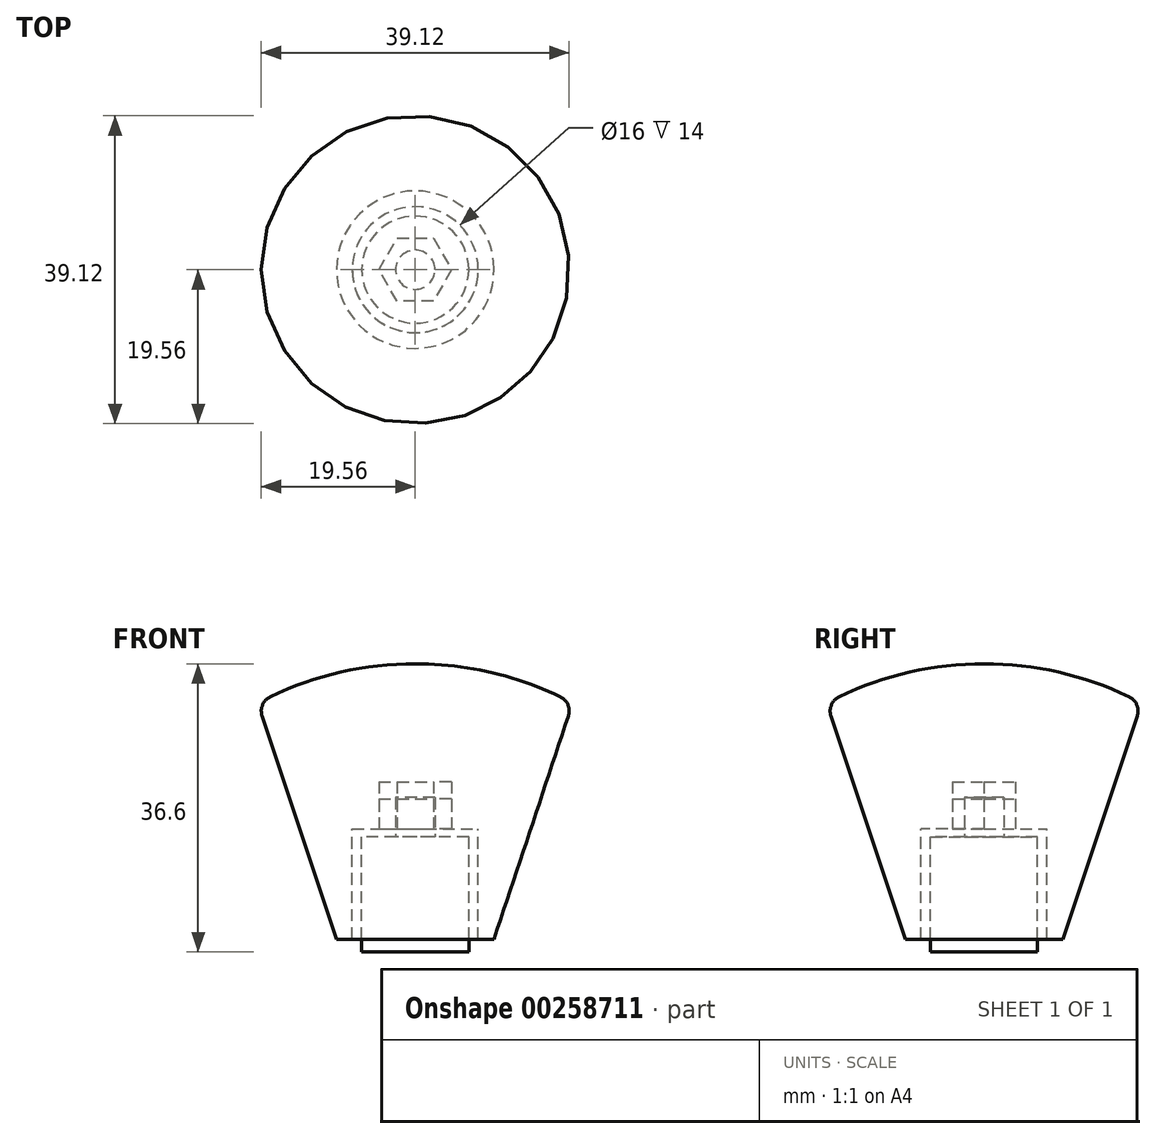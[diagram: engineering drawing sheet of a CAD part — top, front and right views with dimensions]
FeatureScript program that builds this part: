
annotation { "Feature Type Name" : "Feature", "Feature Type Description" : "" }
export const myFeature = defineFeature(function(context is Context, id is Id, definition is map)
    precondition{}
    {
        {
            var Q0;
            Q0=qCreatedBy(makeId("Top.planeOp"),FACE);
            var sketch = newSketch(context, id + "F0", { "sketchPlane" : qUnion([Q0])});
            skCircle(sketch, "E0", {"center": v(0, 0) * mm, "radius": 6.8 * mm});
            skCircle(sketch, "E1", {"center": v(0, 0) * mm, "radius": 2.5 * mm});
            skSolve(sketch);
        }
        {
            var Q0;
            Q0=makeQuery(id+"F0.imprint","IMPRINT",FACE,{"disambiguationData":[TD([[makeQuery(id+"F0.imprint","IMPRINT",EDGE,{"derivedFrom":sQuery(id+"F0.wireOp",EDGE,"E0")}),1.0]])]});
            var Q1;
            Q1=makeQuery(id+"F0.imprint","IMPRINT",FACE,{"disambiguationData":[TD([[makeQuery(id+"F0.imprint","IMPRINT",EDGE,{"derivedFrom":sQuery(id+"F0.wireOp",EDGE,"E1")}),1.0]])]});
            extrude(context, id + "F1", {"entities" : qUnion([Q0, Q1]), "oppositeDirection" : true, "depth" : 14.6 * mm});
        }
        {
            var Q0;
            Q0=makeQuery(id+"F0.imprint","IMPRINT",FACE,{"disambiguationData":[TD([[makeQuery(id+"F0.imprint","IMPRINT",EDGE,{"derivedFrom":sQuery(id+"F0.wireOp",EDGE,"E1")}),1.0]])]});
            extrude(context, id + "F2", {"entities" : qUnion([Q0]), "operationType" : NewBodyOperationType.ADD, "depth" : 5 * mm});
        }
        {
            var Q0;
            Q0=makeQuery(id+"F0.imprint","IMPRINT",FACE,{"disambiguationData":[TD([[makeQuery(id+"F0.imprint","IMPRINT",EDGE,{"derivedFrom":sQuery(id+"F0.wireOp",EDGE,"E0")}),1.0]])]});
            cPlane(context, id + "F3", {"entities" : qUnion([Q0]), "cplaneType" : CPlaneType.OFFSET, "offset" : 1 * mm, "width" : 150 * mm, "height" : 150 * mm});
        }
        {
            var Q0;
            Q0=qCreatedBy(id+"F3.planeOp",FACE);
            var sketch = newSketch(context, id + "F4", { "sketchPlane" : qUnion([Q0])});
            skCircle(sketch, "E2.cCircle", {"center": v(0, 0) * mm, "radius": 4 * mm, "construction": true});
            skLineSegment(sketch, "E2.0", {"start": v(-2.3, 4) * mm, "end": v(2.3, 4) * mm});
            skLineSegment(sketch, "E2.1", {"start": v(2.3, 4) * mm, "end": v(4.62, 0) * mm});
            skLineSegment(sketch, "E2.2", {"start": v(4.62, 0) * mm, "end": v(2.3, -4) * mm});
            skLineSegment(sketch, "E2.3", {"start": v(2.3, -4) * mm, "end": v(-2.3, -4) * mm});
            skLineSegment(sketch, "E2.4", {"start": v(-2.3, -4) * mm, "end": v(-4.62, 0) * mm});
            skLineSegment(sketch, "E2.5", {"start": v(-4.62, 0) * mm, "end": v(-2.3, 4) * mm});
            skPoint(sketch, "E2.0.midPoint", {"position": v(0, 4) * mm});
            skSolve(sketch);
        }
        {
            var Q0;
            Q0=makeQuery(id+"F4.imprint","IMPRINT",FACE,{"disambiguationData":[TD([[makeQuery(id+"F4.imprint","IMPRINT",EDGE,{"derivedFrom":sQuery(id+"F4.wireOp",EDGE,"E2.0")}),-1.0]])]});
            extrude(context, id + "F5", {"entities" : qUnion([Q0]), "depth" : 3.8 * mm});
        }
        {
            var Q0;
            Q0=makeQuery(id+"F5.opExtrude","CAP_FACE",FACE,{"disambiguationData":[OSD([sQuery(id+"F4.wireOp",EDGE,"E2.0"),sQuery(id+"F4.wireOp",EDGE,"E2.1"),sQuery(id+"F4.wireOp",EDGE,"E2.2"),sQuery(id+"F4.wireOp",EDGE,"E2.3"),sQuery(id+"F4.wireOp",EDGE,"E2.4"),sQuery(id+"F4.wireOp",EDGE,"E2.5")])],"isStart":true});
            var sketch = newSketch(context, id + "F6", { "sketchPlane" : qUnion([Q0])});
            skLineSegment(sketch, "E3.0.0", {"start": v(-2.3, -4) * mm, "end": v(-4.62, 0) * mm});
            skLineSegment(sketch, "E3.0.1", {"start": v(-4.62, 0) * mm, "end": v(-2.3, 4) * mm});
            skLineSegment(sketch, "E3.0.2", {"start": v(-2.3, 4) * mm, "end": v(2.3, 4) * mm});
            skLineSegment(sketch, "E3.0.3", {"start": v(2.3, 4) * mm, "end": v(4.62, 0) * mm});
            skLineSegment(sketch, "E3.0.4", {"start": v(4.62, 0) * mm, "end": v(2.3, -4) * mm});
            skLineSegment(sketch, "E3.0.5", {"start": v(2.3, -4) * mm, "end": v(-2.3, -4) * mm});
            skCircle(sketch, "E4", {"center": v(0, 0) * mm, "radius": 8 * mm});
            skSolve(sketch);
        }
        {
            var Q0;
            Q0=makeQuery(id+"F6.imprint","IMPRINT",FACE,{"disambiguationData":[TD([[makeQuery(id+"F6.imprint","IMPRINT",EDGE,{"derivedFrom":sQuery(id+"F6.wireOp",EDGE,"E3.0.0")}),-1.0]])]});
            extrude(context, id + "F7", {"entities" : qUnion([Q0]), "oppositeDirection" : true, "depth" : 6 * mm});
        }
        {
            var Q0;
            Q0=makeQuery(id+"F1.opExtrude","CAP_FACE",FACE,{"disambiguationData":[OSD([sQuery(id+"F0.wireOp",EDGE,"E0")])],"isStart":true});
            cPlane(context, id + "F8", {"entities" : qUnion([Q0]), "cplaneType" : CPlaneType.OFFSET, "offset" : 13 * mm, "oppositeDirection" : true, "width" : 150 * mm, "height" : 150 * mm});
        }
        {
            var Q0;
            Q0=qCreatedBy(id+"F8.planeOp",FACE);
            var sketch = newSketch(context, id + "F9", { "sketchPlane" : qUnion([Q0])});
            skCircle(sketch, "E5.0", {"center": v(0, 0) * mm, "radius": 8 * mm});
            skSolve(sketch);
        }
        {
            var Q0;
            Q0=qCreatedBy(makeId("Front.planeOp"),FACE);
            var sketch = newSketch(context, id + "F10", { "sketchPlane" : qUnion([Q0])});
            skLineSegment(sketch, "E6.0", {"start": v(8, 7) * mm, "end": v(-8, 7) * mm});
            skLineSegment(sketch, "E7.0", {"start": v(-8, -13) * mm, "end": v(8, -13) * mm});
            skArc(sketch, "E8", {"start": v(20, 17) * mm, "mid": v(10.3, 20.73) * mm, "end": v(0, 22) * mm});
            skLineSegment(sketch, "E9", {"start": v(0, 26.7) * mm, "end": v(0, -17.97) * mm, "construction": true});
            skLineSegment(sketch, "E10", {"start": v(8, -13) * mm, "end": v(8, 7) * mm});
            skLineSegment(sketch, "E11", {"start": v(-8, 7) * mm, "end": v(-8, -13) * mm});
            skLineSegment(sketch, "E12", {"start": v(8, -13) * mm, "end": v(10, -13) * mm});
            skLineSegment(sketch, "E13", {"start": v(10, -13) * mm, "end": v(20, 17) * mm});
            skPoint(sketch, "E14", {"position": v(0, 22) * mm});
            skLineSegment(sketch, "E15", {"start": v(20, 17) * mm, "end": v(0, 17) * mm, "construction": true});
            skLineSegment(sketch, "E16", {"start": v(0, 22) * mm, "end": v(0, 7) * mm});
            skSolve(sketch);
        }
        {
            var Q0;
            Q0=makeQuery(id+"F10.imprint","IMPRINT",FACE,{"disambiguationData":[TD([[makeQuery(id+"F10.imprint","IMPRINT",EDGE,{"derivedFrom":sQuery(id+"F10.wireOp",EDGE,"E8")}),1.0]])]});
            var Q1;
            Q1=sQuery(id+"F10.wireOp",EDGE,"E9");
            revolve(context, id + "F11", {"operationType" : NewBodyOperationType.ADD, "entities" : qUnion([Q0]), "axis" : qUnion([Q1]), "revolveType" : RevolveType.FULL});
        }
        {
            var Q0;
            Q0=sQuery(id+"F10.wireOp",VERTEX,"E15.end");
            var Q1;
            Q1=sQuery(id+"F10.wireOp",EDGE,"E16");
            cPlane(context, id + "F12", {"entities" : qUnion([Q0, Q1]), "cplaneType" : CPlaneType.LINE_POINT, "offset" : 25 * mm, "width" : 150 * mm, "height" : 150 * mm});
        }
        {
            var Q0;
            Q0=qCreatedBy(id+"F12.planeOp",FACE);
            var sketch = newSketch(context, id + "F13", { "sketchPlane" : qUnion([Q0])});
            skCircle(sketch, "E17.0", {"center": v(0, 0) * mm, "radius": 20 * mm});
            skCircle(sketch, "E18", {"center": v(0, -25) * mm, "radius": 9 * mm});
            skLineSegment(sketch, "E19.anchor1", {"start": v(0, 0) * mm, "end": v(0, -25) * mm, "construction": true});
            skLineSegment(sketch, "E19.anchor2", {"start": v(0, 0) * mm, "end": v(0, -25) * mm, "construction": true});
            skCircle(sketch, "E20.1.0", {"center": v(21.65, -12.5) * mm, "radius": 9 * mm});
            skCircle(sketch, "E20.2.0", {"center": v(21.65, 12.5) * mm, "radius": 9 * mm});
            skCircle(sketch, "E20.3.0", {"center": v(0, 25) * mm, "radius": 9 * mm});
            skCircle(sketch, "E20.4.0", {"center": v(-21.65, 12.5) * mm, "radius": 9 * mm});
            skCircle(sketch, "E20.5.0", {"center": v(-21.65, -12.5) * mm, "radius": 9 * mm});
            skSolve(sketch);
        }
        {
            var Q0;
            {var subQ0=sQuery(id+"F13.wireOp",EDGE,"E20.5.0");var subQ1=sQuery(id+"F13.wireOp",EDGE,"E17.0");var subQ2=makeQuery(id+"F13.imprint","INTERSECT",VERTEX,{"disambiguationData":[OD(0.0)],"derivedFrom":[subQ1,subQ0]});Q0=makeQuery(id+"F13.imprint","IMPRINT",FACE,{"disambiguationData":[TD([[makeQuery(id+"F13.imprint","IMPRINT",EDGE,{"disambiguationData":[TD([[subQ2,-1.0]])],"derivedFrom":subQ1}),-1.0]])]});}
            var Q1;
            {var subQ0=sQuery(id+"F13.wireOp",EDGE,"E18");var subQ1=sQuery(id+"F13.wireOp",EDGE,"E17.0");var subQ2=makeQuery(id+"F13.imprint","INTERSECT",VERTEX,{"disambiguationData":[OD(0.0)],"derivedFrom":[subQ1,subQ0]});Q1=makeQuery(id+"F13.imprint","IMPRINT",FACE,{"disambiguationData":[TD([[makeQuery(id+"F13.imprint","IMPRINT",EDGE,{"disambiguationData":[TD([[subQ2,-1.0]])],"derivedFrom":subQ1}),-1.0]])]});}
            var Q2;
            {var subQ0=sQuery(id+"F13.wireOp",EDGE,"E20.1.0");var subQ1=sQuery(id+"F13.wireOp",EDGE,"E17.0");var subQ2=makeQuery(id+"F13.imprint","INTERSECT",VERTEX,{"disambiguationData":[OD(0.0)],"derivedFrom":[subQ1,subQ0]});Q2=makeQuery(id+"F13.imprint","IMPRINT",FACE,{"disambiguationData":[TD([[makeQuery(id+"F13.imprint","IMPRINT",EDGE,{"disambiguationData":[TD([[subQ2,1.0]])],"derivedFrom":subQ1}),-1.0]])]});}
            var Q3;
            {var subQ0=sQuery(id+"F13.wireOp",EDGE,"E20.2.0");var subQ1=sQuery(id+"F13.wireOp",EDGE,"E17.0");var subQ2=makeQuery(id+"F13.imprint","INTERSECT",VERTEX,{"disambiguationData":[OD(0.0)],"derivedFrom":[subQ1,subQ0]});Q3=makeQuery(id+"F13.imprint","IMPRINT",FACE,{"disambiguationData":[TD([[makeQuery(id+"F13.imprint","IMPRINT",EDGE,{"disambiguationData":[TD([[subQ2,-1.0]])],"derivedFrom":subQ1}),-1.0]])]});}
            var Q4;
            {var subQ0=sQuery(id+"F13.wireOp",EDGE,"E20.3.0");var subQ1=sQuery(id+"F13.wireOp",EDGE,"E17.0");var subQ2=makeQuery(id+"F13.imprint","INTERSECT",VERTEX,{"disambiguationData":[OD(0.0)],"derivedFrom":[subQ1,subQ0]});Q4=makeQuery(id+"F13.imprint","IMPRINT",FACE,{"disambiguationData":[TD([[makeQuery(id+"F13.imprint","IMPRINT",EDGE,{"disambiguationData":[TD([[subQ2,-1.0]])],"derivedFrom":subQ1}),-1.0]])]});}
            var Q5;
            {var subQ0=sQuery(id+"F13.wireOp",EDGE,"E20.4.0");var subQ1=sQuery(id+"F13.wireOp",EDGE,"E17.0");var subQ2=makeQuery(id+"F13.imprint","INTERSECT",VERTEX,{"disambiguationData":[OD(0.0)],"derivedFrom":[subQ1,subQ0]});Q5=makeQuery(id+"F13.imprint","IMPRINT",FACE,{"disambiguationData":[TD([[makeQuery(id+"F13.imprint","IMPRINT",EDGE,{"disambiguationData":[TD([[subQ2,-1.0]])],"derivedFrom":subQ1}),-1.0]])]});}
            extrude(context, id + "F14", {"entities" : qUnion([Q0, Q1, Q2, Q3, Q4, Q5]), "operationType" : NewBodyOperationType.REMOVE, "endBound" : BoundingType.THROUGH_ALL, "oppositeDirection" : true, "depth" : 25 * mm, "hasSecondDirection" : true, "secondDirectionBound" : SecondDirectionBoundingType.THROUGH_ALL, "secondDirectionOppositeDirection" : false, "secondDirectionDepth" : 25 * mm});
        }
        {
            var Q0;
            Q0=makeQuery(id+"F14.boolean.opBoolean","COPY",FACE,{"derivedFrom":makeQuery(id+"F14.opExtrude","SWEPT_FACE",FACE,{"disambiguationData":[OSD([sQuery(id+"F13.wireOp",EDGE,"E20.3.0")])]})});
            var Q1;
            Q1=makeQuery(id+"F14.boolean.opBoolean","COPY",FACE,{"derivedFrom":makeQuery(id+"F14.opExtrude","SWEPT_FACE",FACE,{"disambiguationData":[OSD([sQuery(id+"F13.wireOp",EDGE,"E20.2.0")])]})});
            var Q2;
            Q2=makeQuery(id+"F14.boolean.opBoolean","COPY",FACE,{"derivedFrom":makeQuery(id+"F14.opExtrude","SWEPT_FACE",FACE,{"disambiguationData":[OSD([sQuery(id+"F13.wireOp",EDGE,"E20.1.0")])]})});
            var Q3;
            Q3=makeQuery(id+"F14.boolean.opBoolean","COPY",FACE,{"derivedFrom":makeQuery(id+"F14.opExtrude","SWEPT_FACE",FACE,{"disambiguationData":[OSD([sQuery(id+"F13.wireOp",EDGE,"E18")])]})});
            var Q4;
            Q4=makeQuery(id+"F14.boolean.opBoolean","COPY",FACE,{"derivedFrom":makeQuery(id+"F14.opExtrude","SWEPT_FACE",FACE,{"disambiguationData":[OSD([sQuery(id+"F13.wireOp",EDGE,"E20.5.0")])]})});
            var Q5;
            Q5=makeQuery(id+"F14.boolean.opBoolean","COPY",FACE,{"derivedFrom":makeQuery(id+"F14.opExtrude","SWEPT_FACE",FACE,{"disambiguationData":[OSD([sQuery(id+"F13.wireOp",EDGE,"E20.4.0")])]})});
            var Q6;
            Q6=makeQuery(id+"F11.opRevolve","SWEPT_FACE",FACE,{"disambiguationData":[OSD([sQuery(id+"F10.wireOp",EDGE,"E8")])]});
            fillet(context, id + "F15", {"entities" : qUnion([Q0, Q1, Q2, Q3, Q4, Q5, Q6]), "radius" : 2 * mm, "tangentPropagation" : true, "allowEdgeOverflow" : false});
        }
    });
